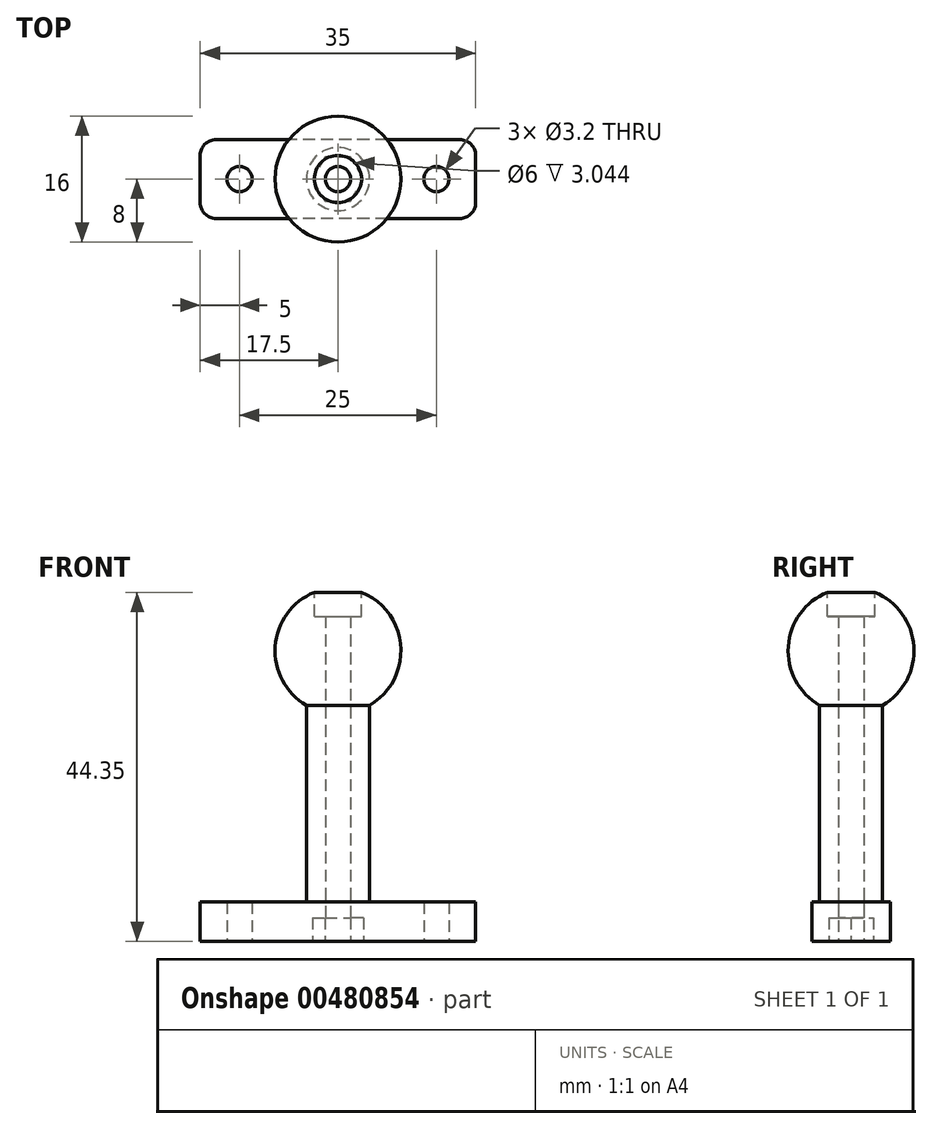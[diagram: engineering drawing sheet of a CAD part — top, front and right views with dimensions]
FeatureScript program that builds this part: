
annotation { "Feature Type Name" : "Feature", "Feature Type Description" : "" }
export const myFeature = defineFeature(function(context is Context, id is Id, definition is map)
    precondition{}
    {
        {
            var Q0;
            Q0=qCreatedBy(makeId("Front.planeOp"),FACE);
            var sketch = newSketch(context, id + "F0", { "sketchPlane" : qUnion([Q0])});
            skLineSegment(sketch, "E0", {"start": v(0, 55.43) * mm, "end": v(0, -68.75) * mm, "construction": true});
            skSolve(sketch);
        }
        {
            var Q0;
            Q0=qCreatedBy(makeId("Front.planeOp"),FACE);
            var sketch = newSketch(context, id + "F1", { "sketchPlane" : qUnion([Q0])});
            skLineSegment(sketch, "E1.top", {"start": v(-4, -31.93) * mm, "end": v(0, -31.93) * mm});
            skLineSegment(sketch, "E1.left", {"start": v(-4, -6.93) * mm, "end": v(-4, -31.93) * mm});
            skArc(sketch, "E2", {"start": v(0, 8) * mm, "mid": v(-7.73, 2.07) * mm, "end": v(-4, -6.93) * mm});
            skLineSegment(sketch, "E3", {"start": v(0, 8) * mm, "end": v(0, -31.93) * mm});
            skSolve(sketch);
        }
        {
            var Q0;
            Q0=makeQuery(id+"F1.imprint","IMPRINT",FACE,{"disambiguationData":[TD([[makeQuery(id+"F1.imprint","IMPRINT",EDGE,{"derivedFrom":sQuery(id+"F1.wireOp",EDGE,"E1.top")}),1.0]])]});
            var Q1;
            Q1=sQuery(id+"F0.wireOp",EDGE,"E0");
            revolve(context, id + "F2", {"entities" : qUnion([Q0]), "axis" : qUnion([Q1]), "revolveType" : RevolveType.FULL});
        }
        {
            var Q0;
            Q0=makeQuery(id+"F2.opRevolve","SWEPT_FACE",FACE,{"disambiguationData":[OSD([sQuery(id+"F1.wireOp",EDGE,"E1.top")])]});
            var sketch = newSketch(context, id + "F3", { "sketchPlane" : qUnion([Q0])});
            skCircle(sketch, "E4", {"center": v(0, 0) * mm, "radius": 1.55 * mm});
            skSolve(sketch);
        }
        {
            var Q0;
            Q0=makeQuery(id+"F2.opRevolve","SWEPT_FACE",FACE,{"disambiguationData":[OSD([sQuery(id+"F1.wireOp",EDGE,"E1.top")])]});
            var sketch = newSketch(context, id + "F4", { "sketchPlane" : qUnion([Q0])});
            skLineSegment(sketch, "E5.bottom", {"start": v(17.5, -5) * mm, "end": v(-17.5, -5) * mm});
            skLineSegment(sketch, "E5.top", {"start": v(17.5, 5) * mm, "end": v(-17.5, 5) * mm});
            skLineSegment(sketch, "E5.left", {"start": v(17.5, -5) * mm, "end": v(17.5, 5) * mm});
            skLineSegment(sketch, "E5.right", {"start": v(-17.5, -5) * mm, "end": v(-17.5, 5) * mm});
            skPoint(sketch, "E5.middle", {"position": v(0, 0) * mm});
            skSolve(sketch);
        }
        {
            var Q0;
            {var subQ0=sQuery(id+"F4.wireOp",EDGE,"E5.left");Q0=makeQuery(id+"F4.imprint","IMPRINT",FACE,{"disambiguationData":[TD([[makeQuery(id+"F4.imprint","IMPRINT",EDGE,{"derivedFrom":subQ0}),1.0]])]});}
            var Q1;
            {var subQ0=sQuery(id+"F4.wireOp",EDGE,"E5.right");Q1=makeQuery(id+"F4.imprint","IMPRINT",FACE,{"disambiguationData":[TD([[makeQuery(id+"F4.imprint","IMPRINT",EDGE,{"derivedFrom":subQ0}),-1.0]])]});}
            var Q2;
            Q2=makeQuery(id+"F4.imprint","IMPRINT",FACE,{"disambiguationData":[TD([[makeQuery(id+"F4.imprint","IMPRINT",EDGE,{"derivedFrom":makeQuery(id+"FwQQhZNau8PPR9i_1.boolean.opBoolean","COPY",EDGE,{"derivedFrom":makeQuery(id+"FwQQhZNau8PPR9i_1.opExtrude","CAP_EDGE",EDGE,{"disambiguationData":[OSD([sQuery(id+"F3.wireOp",EDGE,"E4")])],"isStart":true})})}),-1.0]])]});
            var Q3;
            Q3=makeQuery(id+"F3.imprint","IMPRINT",FACE,{"disambiguationData":[TD([[makeQuery(id+"F3.imprint","IMPRINT",EDGE,{"derivedFrom":sQuery(id+"F3.wireOp",EDGE,"E4")}),1.0]])]});
            var Q4;
            Q4=makeQuery(id+"F3.imprint","IMPRINT",FACE,{"disambiguationData":[TD([[makeQuery(id+"F3.imprint","IMPRINT",EDGE,{"derivedFrom":sQuery(id+"F3.wireOp",EDGE,"E4")}),-1.0]])]});
            extrude(context, id + "F5", {"entities" : qUnion([Q0, Q1, Q2, Q3, Q4]), "operationType" : NewBodyOperationType.ADD, "depth" : 5 * mm, "offsetDistance" : 25 * mm});
        }
        {
            var Q0;
            Q0=makeQuery(id+"F2.opRevolve","SWEPT_EDGE",EDGE,{"disambiguationData":[OSD([sQuery(id+"F1.wireOp",EDGE,"E1.top"),sQuery(id+"F1.wireOp",EDGE,"E1.left")])]});
            var Q1;
            Q1=makeQuery(id+"F5.opExtrude","SWEPT_EDGE",EDGE,{"disambiguationData":[OSD([sQuery(id+"F4.wireOp",EDGE,"E5.bottom"),sQuery(id+"F4.wireOp",EDGE,"E5.right")])]});
            var Q2;
            Q2=makeQuery(id+"F5.opExtrude","SWEPT_EDGE",EDGE,{"disambiguationData":[OSD([sQuery(id+"F4.wireOp",EDGE,"E5.top"),sQuery(id+"F4.wireOp",EDGE,"E5.right")])]});
            var Q3;
            Q3=makeQuery(id+"F5.opExtrude","SWEPT_EDGE",EDGE,{"disambiguationData":[OSD([sQuery(id+"F4.wireOp",EDGE,"E5.top"),sQuery(id+"F4.wireOp",EDGE,"E5.left")])]});
            var Q4;
            Q4=makeQuery(id+"F5.opExtrude","SWEPT_EDGE",EDGE,{"disambiguationData":[OSD([sQuery(id+"F4.wireOp",EDGE,"E5.bottom"),sQuery(id+"F4.wireOp",EDGE,"E5.left")])]});
            fillet(context, id + "F6", {"entities" : qUnion([Q0, Q1, Q2, Q3, Q4]), "radius" : 2 * mm, "tangentPropagation" : true, "allowEdgeOverflow" : false});
        }
        {
            var Q0;
            {var subQ0=sQuery(id+"F1.wireOp",EDGE,"E1.left");var subQ1=sQuery(id+"F1.wireOp",EDGE,"E1.top");Q0=makeQuery(id+"F5.boolean.opBoolean","MERGE",FACE,{"derivedFrom":[makeQuery(id+"F5.opExtrude","CAP_FACE",FACE,{"disambiguationData":[OSD([subQ1,subQ0])],"isStart":false}),makeQuery(id+"F5.opExtrude","CAP_FACE",FACE,{"disambiguationData":[OSD([subQ1,subQ0,sQuery(id+"F4.wireOp",EDGE,"E5.bottom"),sQuery(id+"F4.wireOp",EDGE,"E5.top"),sQuery(id+"F4.wireOp",EDGE,"E5.left"),sQuery(id+"F4.wireOp",EDGE,"E5.right")])],"isStart":false})]});}
            var sketch = newSketch(context, id + "F7", { "sketchPlane" : qUnion([Q0])});
            skLineSegment(sketch, "E6", {"start": v(-19.52, 0) * mm, "end": v(18.72, 0) * mm, "construction": true});
            skCircle(sketch, "E7", {"center": v(-12.5, 0) * mm, "radius": 1.6 * mm});
            skCircle(sketch, "E8", {"center": v(12.5, 0) * mm, "radius": 1.6 * mm});
            skSolve(sketch);
        }
        {
            var Q0;
            Q0=makeQuery(id+"F7.imprint","IMPRINT",FACE,{"disambiguationData":[TD([[makeQuery(id+"F7.imprint","IMPRINT",EDGE,{"derivedFrom":sQuery(id+"F7.wireOp",EDGE,"E7")}),1.0]])]});
            var Q1;
            Q1=makeQuery(id+"F7.imprint","IMPRINT",FACE,{"disambiguationData":[TD([[makeQuery(id+"F7.imprint","IMPRINT",EDGE,{"derivedFrom":sQuery(id+"F7.wireOp",EDGE,"E8")}),1.0]])]});
            extrude(context, id + "F8", {"entities" : qUnion([Q0, Q1]), "operationType" : NewBodyOperationType.REMOVE, "oppositeDirection" : true, "depth" : 6 * mm, "offsetDistance" : 25 * mm});
        }
        {
            var Q0;
            {var subQ0=sQuery(id+"F1.wireOp",EDGE,"E1.left");var subQ1=sQuery(id+"F1.wireOp",EDGE,"E1.top");Q0=makeQuery(id+"F5.boolean.opBoolean","MERGE",FACE,{"derivedFrom":[makeQuery(id+"F5.opExtrude","CAP_FACE",FACE,{"disambiguationData":[OSD([subQ1,subQ0])],"isStart":false}),makeQuery(id+"F5.opExtrude","CAP_FACE",FACE,{"disambiguationData":[OSD([subQ1,subQ0,sQuery(id+"F4.wireOp",EDGE,"E5.bottom"),sQuery(id+"F4.wireOp",EDGE,"E5.top"),sQuery(id+"F4.wireOp",EDGE,"E5.left"),sQuery(id+"F4.wireOp",EDGE,"E5.right")])],"isStart":false})]});}
            var sketch = newSketch(context, id + "F9", { "sketchPlane" : qUnion([Q0])});
            skCircle(sketch, "E9", {"center": v(0, 0) * mm, "radius": 1.6 * mm});
            skCircle(sketch, "E10.cCircle", {"center": v(0, 0) * mm, "radius": 3.25 * mm, "construction": true});
            skLineSegment(sketch, "E10.0", {"start": v(3.25, 0) * mm, "end": v(1.63, -2.81) * mm});
            skLineSegment(sketch, "E10.1", {"start": v(1.63, -2.81) * mm, "end": v(-1.62, -2.81) * mm});
            skLineSegment(sketch, "E10.2", {"start": v(-1.62, -2.81) * mm, "end": v(-3.25, 0) * mm});
            skLineSegment(sketch, "E10.3", {"start": v(-3.25, 0) * mm, "end": v(-1.63, 2.81) * mm});
            skLineSegment(sketch, "E10.4", {"start": v(-1.63, 2.81) * mm, "end": v(1.62, 2.81) * mm});
            skLineSegment(sketch, "E10.5", {"start": v(1.62, 2.81) * mm, "end": v(3.25, 0) * mm});
            skSolve(sketch);
        }
        {
            var Q0;
            Q0=makeQuery(id+"F9.imprint","IMPRINT",FACE,{"disambiguationData":[TD([[makeQuery(id+"F9.imprint","IMPRINT",EDGE,{"derivedFrom":sQuery(id+"F9.wireOp",EDGE,"E9")}),1.0]])]});
            extrude(context, id + "F10", {"entities" : qUnion([Q0]), "operationType" : NewBodyOperationType.REMOVE, "oppositeDirection" : true, "depth" : 50 * mm, "offsetDistance" : 25 * mm});
        }
        {
            var Q0;
            Q0=makeQuery(id+"F9.imprint","IMPRINT",FACE,{"disambiguationData":[TD([[makeQuery(id+"F9.imprint","IMPRINT",EDGE,{"derivedFrom":sQuery(id+"F9.wireOp",EDGE,"E9")}),-1.0]])]});
            extrude(context, id + "F11", {"entities" : qUnion([Q0]), "operationType" : NewBodyOperationType.REMOVE, "oppositeDirection" : true, "depth" : 3 * mm, "offsetDistance" : 25 * mm});
        }
        {
            var Q0;
            Q0=makeQuery(id+"F9.imprint","IMPRINT",FACE,{"disambiguationData":[TD([[makeQuery(id+"F9.imprint","IMPRINT",EDGE,{"derivedFrom":sQuery(id+"F9.wireOp",EDGE,"E10.0")}),1.0]])]});
            cPlane(context, id + "F12", {"entities" : qUnion([Q0]), "cplaneType" : CPlaneType.OFFSET, "offset" : 44.8 * mm, "oppositeDirection" : true, "width" : 150 * mm, "height" : 150 * mm});
        }
        {
            var Q0;
            Q0=qCreatedBy(id+"F12.planeOp",FACE);
            var sketch = newSketch(context, id + "F13", { "sketchPlane" : qUnion([Q0])});
            skCircle(sketch, "E11", {"center": v(0, 0) * mm, "radius": 3 * mm});
            skSolve(sketch);
        }
        {
            var Q0;
            Q0 = qSketchRegion(id + "F13", true);
            extrude(context, id + "F14", {"entities" : qUnion([Q0]), "operationType" : NewBodyOperationType.REMOVE, "depth" : 3.5 * mm, "offsetDistance" : 25 * mm});
        }
    });
